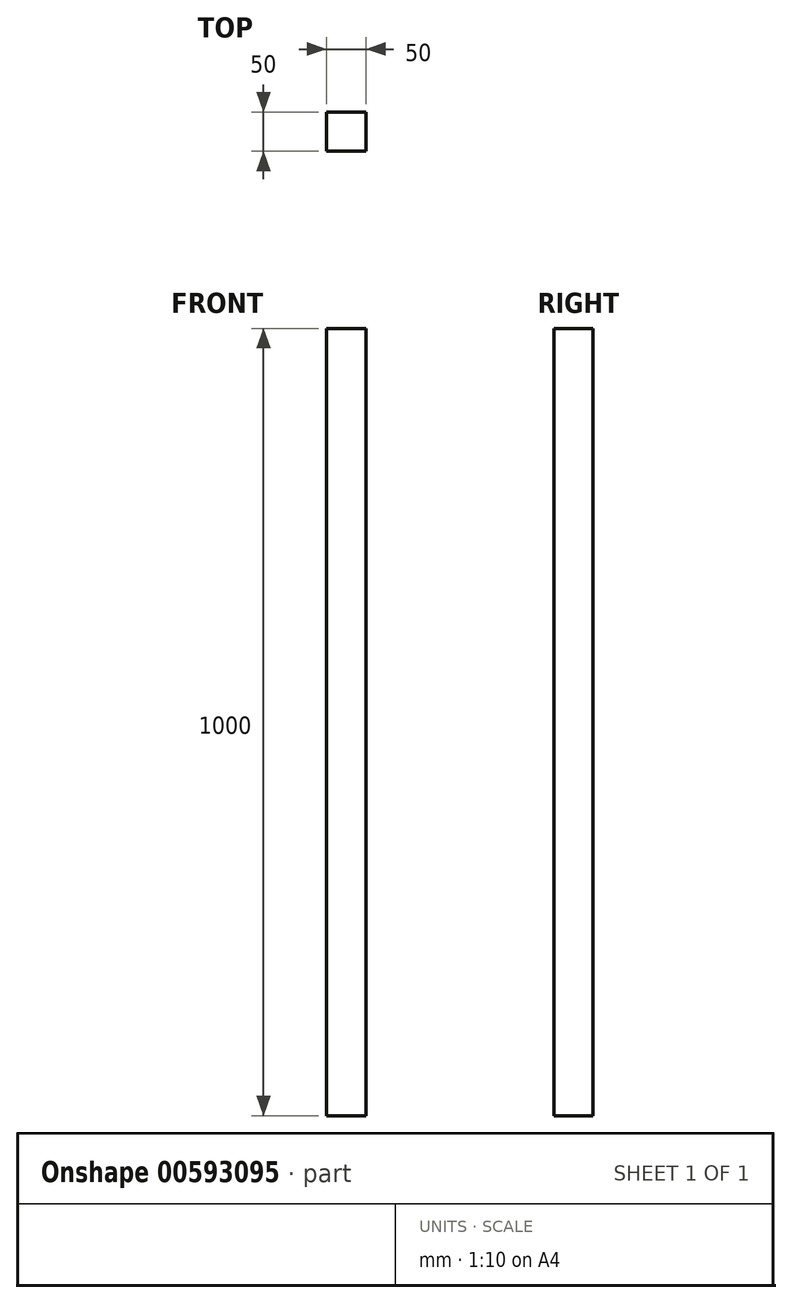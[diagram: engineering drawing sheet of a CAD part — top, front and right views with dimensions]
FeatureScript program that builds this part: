
annotation { "Feature Type Name" : "Feature", "Feature Type Description" : "" }
export const myFeature = defineFeature(function(context is Context, id is Id, definition is map)
    precondition{}
    {
        {
            var Q0;
            Q0=qCreatedBy(makeId("Top.planeOp"),FACE);
            var sketch = newSketch(context, id + "F0", { "sketchPlane" : qUnion([Q0])});
            skLineSegment(sketch, "E0.bottom", {"start": v(25, 25) * mm, "end": v(-25, 25) * mm});
            skLineSegment(sketch, "E0.top", {"start": v(25, -25) * mm, "end": v(-25, -25) * mm});
            skLineSegment(sketch, "E0.left", {"start": v(25, 25) * mm, "end": v(25, -25) * mm});
            skLineSegment(sketch, "E0.right", {"start": v(-25, 25) * mm, "end": v(-25, -25) * mm});
            skPoint(sketch, "E0.middle", {"position": v(0, 0) * mm});
            skSolve(sketch);
        }
        {
            var Q0;
            Q0=makeQuery(id+"F0.imprint","IMPRINT",FACE,{"disambiguationData":[TD([[makeQuery(id+"F0.imprint","IMPRINT",EDGE,{"derivedFrom":sQuery(id+"F0.wireOp",EDGE,"E0.bottom")}),1.0]])]});
            extrude(context, id + "F1", {"entities" : qUnion([Q0]), "depth" : 1000 * mm, "offsetDistance" : 25 * mm});
        }
    });
